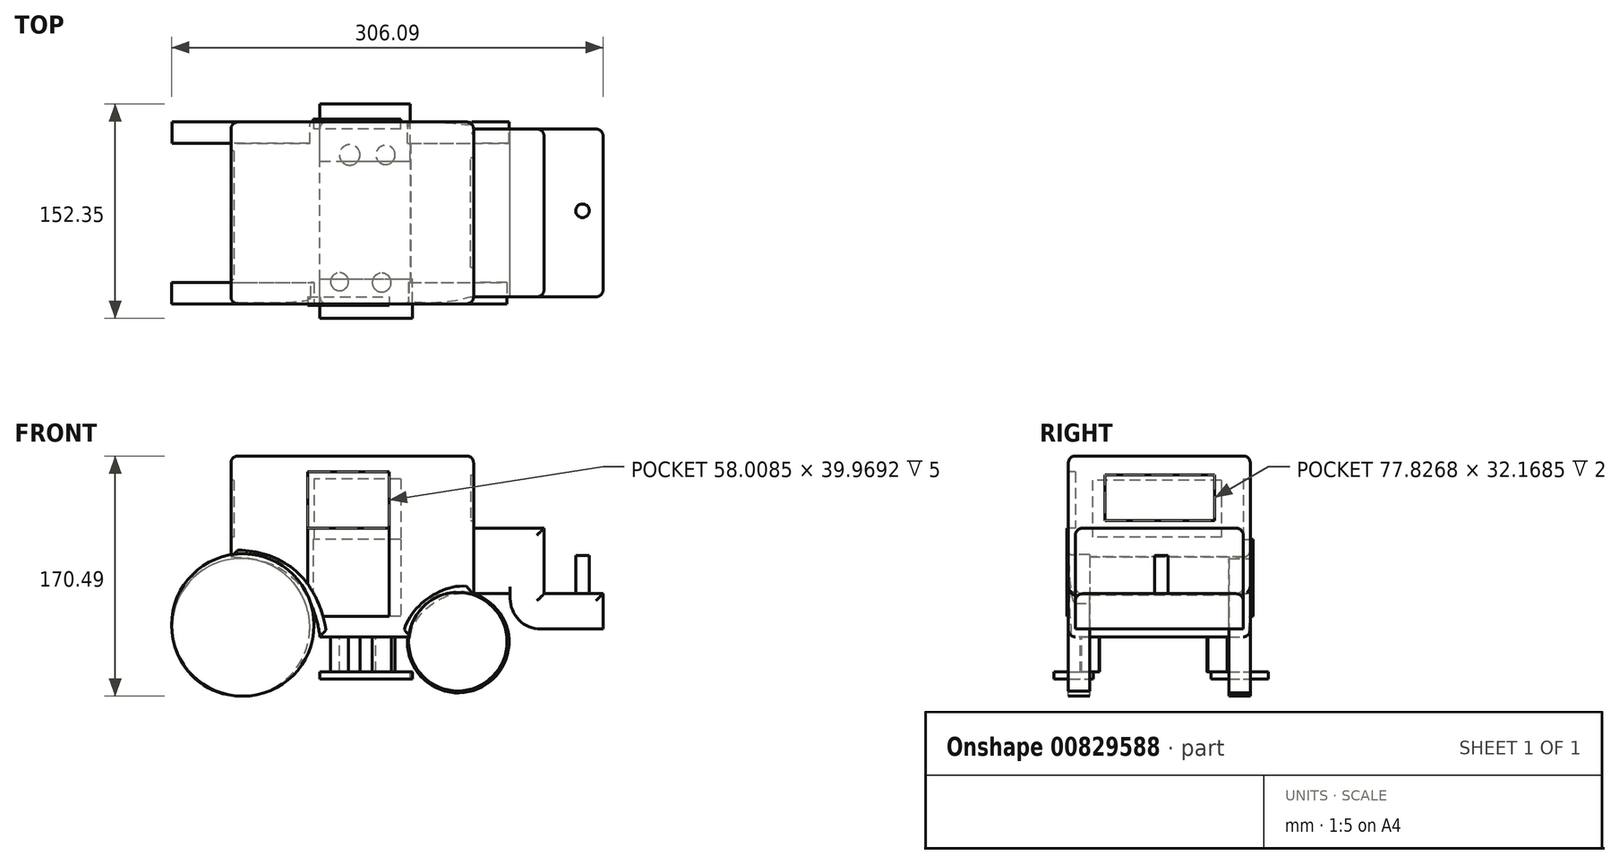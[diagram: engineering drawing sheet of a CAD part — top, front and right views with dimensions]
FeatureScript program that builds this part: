
annotation { "Feature Type Name" : "Feature", "Feature Type Description" : "" }
export const myFeature = defineFeature(function(context is Context, id is Id, definition is map)
    precondition{}
    {
        {
            var Q0;
            Q0=qCreatedBy(makeId("Front.planeOp"),FACE);
            var sketch = newSketch(context, id + "F0", { "sketchPlane" : qUnion([Q0])});
            skLineSegment(sketch, "E0.bottom", {"start": v(-63.14, 51.22) * mm, "end": v(108.92, 51.22) * mm});
            skLineSegment(sketch, "E0.top", {"start": v(-63.14, -77.13) * mm, "end": v(108.92, -77.13) * mm});
            skLineSegment(sketch, "E0.left", {"start": v(-63.14, 51.22) * mm, "end": v(-63.14, -77.13) * mm});
            skLineSegment(sketch, "E0.right", {"start": v(108.92, 51.22) * mm, "end": v(108.92, -77.13) * mm});
            skFitSpline(sketch, "E1", {"points": [v(-63.14, -20.5) * mm, v(0, -77.13) * mm], "startDerivative": vector(140.08, 1.65) * mm, "endDerivative": vector(9.7, -72.66) * mm});
            skCircle(sketch, "E2", {"center": v(-56, -70.4) * mm, "radius": 48.82 * mm});
            skFitSpline(sketch, "E3", {"points": [v(64.44, -77.13) * mm, v(108.92, -47.47) * mm], "startDerivative": vector(-2.62, 44.49) * mm, "endDerivative": vector(57.47, -20.94) * mm});
            skSolve(sketch);
        }
        {
            var Q0;
            {var subQ3=sQuery(id+"F0.wireOp",EDGE,"E1");Q0=makeQuery(id+"F0.imprint","IMPRINT",FACE,{"disambiguationData":[TD([[makeQuery(id+"F0.imprint","IMPRINT",EDGE,{"derivedFrom":subQ3}),-1.0]])]});}
            var Q1;
            {var subQ1=sQuery(id+"F0.wireOp",EDGE,"E0.bottom");Q1=makeQuery(id+"F0.imprint","IMPRINT",FACE,{"disambiguationData":[TD([[makeQuery(id+"F0.imprint","IMPRINT",EDGE,{"derivedFrom":subQ1}),-1.0]])]});}
            extrude(context, id + "F1", {"entities" : qUnion([Q0, Q1]), "depth" : 129 * mm, "offsetDistance" : 25 * mm});
        }
        {
            var Q0;
            {var subQ3=sQuery(id+"F0.wireOp",EDGE,"E1");Q0=makeQuery(id+"F0.imprint","IMPRINT",FACE,{"disambiguationData":[TD([[makeQuery(id+"F0.imprint","IMPRINT",EDGE,{"derivedFrom":subQ3}),-1.0]])]});}
            extrude(context, id + "F2", {"entities" : qUnion([Q0]), "operationType" : NewBodyOperationType.REMOVE, "depth" : 218 * mm, "offsetDistance" : 25 * mm});
        }
        {
            var Q0;
            Q0=makeQuery(id+"F1.opExtrude","CAP_FACE",FACE,{"disambiguationData":[OSD([sQuery(id+"F0.wireOp",EDGE,"E0.bottom"),sQuery(id+"F0.wireOp",EDGE,"E0.top"),sQuery(id+"F0.wireOp",EDGE,"E0.left"),sQuery(id+"F0.wireOp",EDGE,"E0.right")])],"isStart":true});
            fillet(context, id + "F3", {"entities" : qUnion([Q0]), "radius" : 5 * mm, "tangentPropagation" : true, "allowEdgeOverflow" : false});
        }
        {
            var Q0;
            Q0=makeQuery(id+"F1.opExtrude","CAP_FACE",FACE,{"disambiguationData":[OSD([sQuery(id+"F0.wireOp",EDGE,"E0.bottom"),sQuery(id+"F0.wireOp",EDGE,"E0.top"),sQuery(id+"F0.wireOp",EDGE,"E0.left"),sQuery(id+"F0.wireOp",EDGE,"E0.right")])],"isStart":false});
            fillet(context, id + "F4", {"entities" : qUnion([Q0]), "radius" : 5 * mm, "tangentPropagation" : true, "allowEdgeOverflow" : false});
        }
        {
            var Q0;
            Q0=makeQuery(id+"F1.opExtrude","SWEPT_FACE",FACE,{"disambiguationData":[OSD([sQuery(id+"F0.wireOp",EDGE,"E0.bottom")])]});
            fillet(context, id + "F5", {"entities" : qUnion([Q0]), "radius" : 5 * mm, "tangentPropagation" : true, "allowEdgeOverflow" : false});
        }
        {
            var Q0;
            {var subQ0=sQuery(id+"F0.wireOp",EDGE,"E0.left");var subQ1=sQuery(id+"F0.wireOp",EDGE,"E0.top");var subQ2=makeQuery(id+"F0.imprint","INTERSECT",VERTEX,{"derivedFrom":[subQ1,subQ0]});Q0=makeQuery(id+"F0.imprint","IMPRINT",FACE,{"disambiguationData":[TD([[makeQuery(id+"F0.imprint","IMPRINT",EDGE,{"disambiguationData":[TD([[subQ2,-1.0]])],"derivedFrom":subQ1}),-1.0]])]});}
            var Q1;
            {var subQ0=sQuery(id+"F0.wireOp",EDGE,"E0.left");var subQ1=sQuery(id+"F0.wireOp",EDGE,"E0.top");var subQ2=makeQuery(id+"F0.imprint","INTERSECT",VERTEX,{"derivedFrom":[subQ1,subQ0]});Q1=makeQuery(id+"F0.imprint","IMPRINT",FACE,{"disambiguationData":[TD([[makeQuery(id+"F0.imprint","IMPRINT",EDGE,{"disambiguationData":[TD([[subQ2,-1.0]])],"derivedFrom":subQ1}),1.0]])]});}
            extrude(context, id + "F6", {"entities" : qUnion([Q0, Q1]), "depth" : 15 * mm, "offsetDistance" : 25 * mm});
        }
        {
            var Q0;
            Q0=qCreatedBy(makeId("Front.planeOp"),FACE);
            var sketch = newSketch(context, id + "F7", { "sketchPlane" : qUnion([Q0])});
            skCircle(sketch, "E4", {"center": v(98.04, -80.89) * mm, "radius": 36 * mm});
            skSolve(sketch);
        }
        {
            var Q0;
            Q0=makeQuery(id+"F7.imprint","IMPRINT",FACE,{"disambiguationData":[TD([[makeQuery(id+"F7.imprint","IMPRINT",EDGE,{"derivedFrom":sQuery(id+"F7.wireOp",EDGE,"E4")}),1.0]])]});
            extrude(context, id + "F8", {"entities" : qUnion([Q0]), "operationType" : NewBodyOperationType.ADD, "depth" : 15 * mm, "offsetDistance" : 25 * mm});
        }
        {
            var Q0;
            Q0=makeQuery(id+"F1.opExtrude","CAP_FACE",FACE,{"disambiguationData":[OSD([sQuery(id+"F0.wireOp",EDGE,"E0.bottom"),sQuery(id+"F0.wireOp",EDGE,"E0.top"),sQuery(id+"F0.wireOp",EDGE,"E0.left"),sQuery(id+"F0.wireOp",EDGE,"E0.right"),sQuery(id+"F0.wireOp",EDGE,"E2"),sQuery(id+"F0.wireOp",EDGE,"E3")])],"isStart":false});
            var sketch = newSketch(context, id + "F9", { "sketchPlane" : qUnion([Q0])});
            skCircle(sketch, "E5", {"center": v(-54.73, -68.73) * mm, "radius": 50.55 * mm});
            skSolve(sketch);
        }
        {
            var Q0;
            Q0=makeQuery(id+"F9.imprint","IMPRINT",FACE,{"disambiguationData":[TD([[makeQuery(id+"F9.imprint","IMPRINT",EDGE,{"derivedFrom":sQuery(id+"F9.wireOp",EDGE,"E5")}),1.0]])]});
            extrude(context, id + "F10", {"entities" : qUnion([Q0]), "operationType" : NewBodyOperationType.ADD, "oppositeDirection" : true, "depth" : 15 * mm, "offsetDistance" : 25 * mm});
        }
        {
            var Q0;
            Q0=makeQuery(id+"F1.opExtrude","CAP_FACE",FACE,{"disambiguationData":[OSD([sQuery(id+"F0.wireOp",EDGE,"E0.bottom"),sQuery(id+"F0.wireOp",EDGE,"E0.top"),sQuery(id+"F0.wireOp",EDGE,"E0.left"),sQuery(id+"F0.wireOp",EDGE,"E0.right"),sQuery(id+"F0.wireOp",EDGE,"E2"),sQuery(id+"F0.wireOp",EDGE,"E3")])],"isStart":false});
            var sketch = newSketch(context, id + "F11", { "sketchPlane" : qUnion([Q0])});
            skCircle(sketch, "E6", {"center": v(97.8, -80.55) * mm, "radius": 34.93 * mm});
            skSolve(sketch);
        }
        {
            var Q0;
            Q0=makeQuery(id+"F11.imprint","IMPRINT",FACE,{"disambiguationData":[TD([[makeQuery(id+"F11.imprint","IMPRINT",EDGE,{"derivedFrom":sQuery(id+"F11.wireOp",EDGE,"E6")}),1.0]])]});
            extrude(context, id + "F12", {"entities" : qUnion([Q0]), "operationType" : NewBodyOperationType.ADD, "oppositeDirection" : true, "depth" : 15 * mm, "offsetDistance" : 25 * mm});
        }
        {
            var Q0;
            Q0=makeQuery(id+"F1.opExtrude","CAP_FACE",FACE,{"disambiguationData":[OSD([sQuery(id+"F0.wireOp",EDGE,"E0.bottom"),sQuery(id+"F0.wireOp",EDGE,"E0.top"),sQuery(id+"F0.wireOp",EDGE,"E0.left"),sQuery(id+"F0.wireOp",EDGE,"E0.right"),sQuery(id+"F0.wireOp",EDGE,"E2"),sQuery(id+"F0.wireOp",EDGE,"E3")])],"isStart":false});
            var sketch = newSketch(context, id + "F13", { "sketchPlane" : qUnion([Q0])});
            skLineSegment(sketch, "E7.bottom", {"start": v(-8.85, 39.97) * mm, "end": v(49.16, 39.97) * mm});
            skLineSegment(sketch, "E7.top", {"start": v(-8.85, 0) * mm, "end": v(49.16, 0) * mm});
            skLineSegment(sketch, "E7.left", {"start": v(-8.85, 39.97) * mm, "end": v(-8.85, 0) * mm});
            skLineSegment(sketch, "E7.right", {"start": v(49.16, 39.97) * mm, "end": v(49.16, 0) * mm});
            skSolve(sketch);
        }
        {
            var Q0;
            Q0=makeQuery(id+"F13.imprint","IMPRINT",FACE,{"disambiguationData":[TD([[makeQuery(id+"F13.imprint","IMPRINT",EDGE,{"derivedFrom":sQuery(id+"F13.wireOp",EDGE,"E7.bottom")}),-1.0]])]});
            extrude(context, id + "F14", {"entities" : qUnion([Q0]), "operationType" : NewBodyOperationType.REMOVE, "oppositeDirection" : true, "depth" : 5 * mm, "offsetDistance" : 25 * mm});
        }
        {
            var Q0;
            Q0=makeQuery(id+"F1.opExtrude","CAP_FACE",FACE,{"disambiguationData":[OSD([sQuery(id+"F0.wireOp",EDGE,"E0.bottom"),sQuery(id+"F0.wireOp",EDGE,"E0.top"),sQuery(id+"F0.wireOp",EDGE,"E0.left"),sQuery(id+"F0.wireOp",EDGE,"E0.right"),sQuery(id+"F0.wireOp",EDGE,"E2"),sQuery(id+"F0.wireOp",EDGE,"E3")])],"isStart":false});
            var sketch = newSketch(context, id + "F15", { "sketchPlane" : qUnion([Q0])});
            skLineSegment(sketch, "E8", {"start": v(-8.85, 0) * mm, "end": v(-8.85, -39.58) * mm});
            skLineSegment(sketch, "E9", {"start": v(49.16, 0) * mm, "end": v(49.16, -62.53) * mm});
            skLineSegment(sketch, "E10", {"start": v(49.16, -62.53) * mm, "end": v(2.09, -62.53) * mm});
            skSolve(sketch);
        }
        {
            var Q0;
            {var subQ1=sQuery(id+"F15.wireOp",EDGE,"E8");Q0=makeQuery(id+"F15.imprint","IMPRINT",FACE,{"disambiguationData":[TD([[makeQuery(id+"F15.imprint","IMPRINT",EDGE,{"derivedFrom":subQ1}),1.0]])]});}
            extrude(context, id + "F16", {"entities" : qUnion([Q0]), "operationType" : NewBodyOperationType.ADD, "depth" : 1 * mm, "offsetDistance" : 25 * mm});
        }
        {
            var Q0;
            Q0=makeQuery(id+"F1.opExtrude","CAP_FACE",FACE,{"disambiguationData":[OSD([sQuery(id+"F0.wireOp",EDGE,"E0.bottom"),sQuery(id+"F0.wireOp",EDGE,"E0.top"),sQuery(id+"F0.wireOp",EDGE,"E0.left"),sQuery(id+"F0.wireOp",EDGE,"E0.right"),sQuery(id+"F0.wireOp",EDGE,"E2"),sQuery(id+"F0.wireOp",EDGE,"E3")])],"isStart":false});
            var sketch = newSketch(context, id + "F17", { "sketchPlane" : qUnion([Q0])});
            skFitSpline(sketch, "E11", {"points": [v(-58.14, -15.56) * mm, v(-8.85, 39.97) * mm], "startDerivative": vector(207, -25) * mm, "endDerivative": vector(147.87, 73.92) * mm});
            skFitSpline(sketch, "E12", {"points": [v(53.1, 39.97) * mm, v(103.92, -41.26) * mm], "startDerivative": vector(152.47, -4.07) * mm, "endDerivative": vector(89.96, -3.1) * mm});
            skFitSpline(sketch, "E13", {"points": [v(49.16, -62.53) * mm, v(103.92, 0) * mm], "startDerivative": vector(164.3, 21.28) * mm, "endDerivative": vector(164.3, -26.3) * mm});
            skFitSpline(sketch, "E14", {"points": [v(-58.14, 46.22) * mm, v(-8.85, 0) * mm], "startDerivative": vector(107.32, -14.38) * mm, "endDerivative": vector(128.4, 68.32) * mm});
            skFitSpline(sketch, "E15", {"points": [v(49.16, -25.03) * mm, v(103.92, 46.22) * mm], "startDerivative": vector(103.06, -10.14) * mm, "endDerivative": vector(147.4, 54.93) * mm});
            skSolve(sketch);
        }
        {
            var Q0;
            Q0=sQuery(id+"F17.wireOp",EDGE,"E11");
            extrude(context, id + "F18", {"bodyType" : ToolBodyType.SURFACE, "surfaceEntities" : qUnion([Q0]), "depth" : 2 * mm, "offsetDistance" : 25 * mm});
        }
        {
            var Q0;
            Q0=sQuery(id+"F17.wireOp",EDGE,"E14");
            extrude(context, id + "F19", {"bodyType" : ToolBodyType.SURFACE, "surfaceEntities" : qUnion([Q0]), "depth" : 2 * mm, "offsetDistance" : 25 * mm});
        }
        {
            var Q0;
            Q0=sQuery(id+"F17.wireOp",EDGE,"E15");
            extrude(context, id + "F20", {"bodyType" : ToolBodyType.SURFACE, "surfaceEntities" : qUnion([Q0]), "depth" : 2 * mm, "offsetDistance" : 25 * mm});
        }
        {
            var Q0;
            Q0=sQuery(id+"F17.wireOp",EDGE,"E13");
            extrude(context, id + "F21", {"bodyType" : ToolBodyType.SURFACE, "surfaceEntities" : qUnion([Q0]), "depth" : 2 * mm, "offsetDistance" : 25 * mm});
        }
        {
            var Q0;
            Q0=sQuery(id+"F17.wireOp",EDGE,"E12");
            extrude(context, id + "F22", {"bodyType" : ToolBodyType.SURFACE, "surfaceEntities" : qUnion([Q0]), "depth" : 2 * mm, "offsetDistance" : 25 * mm});
        }
        {
            var Q0;
            Q0=makeQuery(id+"F1.opExtrude","SWEPT_FACE",FACE,{"disambiguationData":[OSD([sQuery(id+"F0.wireOp",EDGE,"E0.right")])]});
            var sketch = newSketch(context, id + "F23", { "sketchPlane" : qUnion([Q0])});
            skLineSegment(sketch, "E16.bottom", {"start": v(-124, 0) * mm, "end": v(-5, 0) * mm});
            skLineSegment(sketch, "E16.top", {"start": v(-124, -46.56) * mm, "end": v(-5, -46.56) * mm});
            skLineSegment(sketch, "E16.left", {"start": v(-124, 0) * mm, "end": v(-124, -46.56) * mm});
            skLineSegment(sketch, "E16.right", {"start": v(-5, 0) * mm, "end": v(-5, -46.56) * mm});
            skSolve(sketch);
        }
        {
            var Q0;
            Q0=makeQuery(id+"F23.imprint","IMPRINT",FACE,{"disambiguationData":[TD([[makeQuery(id+"F23.imprint","IMPRINT",EDGE,{"derivedFrom":sQuery(id+"F23.wireOp",EDGE,"E16.bottom")}),-1.0]])]});
            extrude(context, id + "F24", {"entities" : qUnion([Q0]), "operationType" : NewBodyOperationType.ADD, "depth" : 50 * mm, "offsetDistance" : 25 * mm});
        }
        {
            var Q0;
            Q0=makeQuery(id+"F24.opExtrude","SWEPT_FACE",FACE,{"disambiguationData":[OSD([sQuery(id+"F23.wireOp",EDGE,"E16.top")])]});
            var sketch = newSketch(context, id + "F25", { "sketchPlane" : qUnion([Q0])});
            skLineSegment(sketch, "E17.bottom", {"start": v(134.85, 124) * mm, "end": v(200.81, 124) * mm});
            skLineSegment(sketch, "E17.top", {"start": v(134.85, 5) * mm, "end": v(200.81, 5) * mm});
            skLineSegment(sketch, "E17.left", {"start": v(134.85, 124) * mm, "end": v(134.85, 5) * mm});
            skLineSegment(sketch, "E17.right", {"start": v(200.81, 124) * mm, "end": v(200.81, 5) * mm});
            skSolve(sketch);
        }
        {
            var Q0;
            Q0 = qSketchRegion(id + "F25", true);
            extrude(context, id + "F26", {"entities" : qUnion([Q0]), "operationType" : NewBodyOperationType.ADD, "depth" : 25 * mm, "offsetDistance" : 25 * mm});
        }
        {
            var Q0;
            Q0=makeQuery(id+"F26.opExtrude","CAP_EDGE",EDGE,{"disambiguationData":[OSD([sQuery(id+"F25.wireOp",EDGE,"E17.left")])],"isStart":false});
            fillet(context, id + "F27", {"entities" : qUnion([Q0]), "radius" : 21.73 * mm, "tangentPropagation" : true, "allowEdgeOverflow" : false});
        }
        {
            var Q0;
            Q0=makeQuery(id+"F24.opExtrude","SWEPT_EDGE",EDGE,{"disambiguationData":[OSD([sQuery(id+"F0.wireOp",EDGE,"E0.right"),sQuery(id+"F23.wireOp",EDGE,"E16.bottom"),sQuery(id+"F23.wireOp",EDGE,"E16.left")])]});
            var Q1;
            Q1=makeQuery(id+"F24.opExtrude","CAP_EDGE",EDGE,{"disambiguationData":[OSD([sQuery(id+"F23.wireOp",EDGE,"E16.left")])],"isStart":false});
            var Q2;
            Q2=makeQuery(id+"F26.opExtrude","CAP_EDGE",EDGE,{"disambiguationData":[OSD([sQuery(id+"F25.wireOp",EDGE,"E17.bottom")])],"isStart":true});
            var Q3;
            Q3=makeQuery(id+"F26.opExtrude","SWEPT_EDGE",EDGE,{"disambiguationData":[OSD([sQuery(id+"F25.wireOp",EDGE,"E17.bottom"),sQuery(id+"F25.wireOp",EDGE,"E17.right")])]});
            var Q4;
            Q4=makeQuery(id+"F24.opExtrude","SWEPT_EDGE",EDGE,{"disambiguationData":[OSD([sQuery(id+"F0.wireOp",EDGE,"E0.right"),sQuery(id+"F23.wireOp",EDGE,"E16.top"),sQuery(id+"F23.wireOp",EDGE,"E16.left")])]});
            fillet(context, id + "F28", {"entities" : qUnion([Q0, Q1, Q2, Q3, Q4]), "radius" : 5 * mm, "tangentPropagation" : true, "allowEdgeOverflow" : false});
        }
        {
            var Q0;
            Q0=makeQuery(id+"F24.opExtrude","SWEPT_EDGE",EDGE,{"disambiguationData":[OSD([sQuery(id+"F0.wireOp",EDGE,"E0.right"),sQuery(id+"F23.wireOp",EDGE,"E16.bottom"),sQuery(id+"F23.wireOp",EDGE,"E16.right")])]});
            var Q1;
            Q1=makeQuery(id+"F24.opExtrude","CAP_EDGE",EDGE,{"disambiguationData":[OSD([sQuery(id+"F23.wireOp",EDGE,"E16.right")])],"isStart":false});
            var Q2;
            Q2=makeQuery(id+"F26.opExtrude","CAP_EDGE",EDGE,{"disambiguationData":[OSD([sQuery(id+"F25.wireOp",EDGE,"E17.top")])],"isStart":true});
            var Q3;
            Q3=makeQuery(id+"F26.opExtrude","SWEPT_EDGE",EDGE,{"disambiguationData":[OSD([sQuery(id+"F25.wireOp",EDGE,"E17.top"),sQuery(id+"F25.wireOp",EDGE,"E17.right")])]});
            var Q4;
            Q4=makeQuery(id+"F24.opExtrude","SWEPT_EDGE",EDGE,{"disambiguationData":[OSD([sQuery(id+"F23.wireOp",EDGE,"E16.top"),sQuery(id+"F23.wireOp",EDGE,"E16.right")])]});
            fillet(context, id + "F29", {"entities" : qUnion([Q0, Q1, Q2, Q3, Q4]), "radius" : 5 * mm, "tangentPropagation" : true, "allowEdgeOverflow" : false});
        }
        {
            var Q0;
            Q0=makeQuery(id+"F26.opExtrude","CAP_FACE",FACE,{"disambiguationData":[OSD([sQuery(id+"F25.wireOp",EDGE,"E17.bottom"),sQuery(id+"F25.wireOp",EDGE,"E17.top"),sQuery(id+"F25.wireOp",EDGE,"E17.left"),sQuery(id+"F25.wireOp",EDGE,"E17.right")])],"isStart":true});
            var sketch = newSketch(context, id + "F30", { "sketchPlane" : qUnion([Q0])});
            skCircle(sketch, "E18", {"center": v(186.19, -62.99) * mm, "radius": 4.82 * mm});
            skSolve(sketch);
        }
        {
            var Q0;
            Q0=makeQuery(id+"F30.imprint","IMPRINT",FACE,{"disambiguationData":[TD([[makeQuery(id+"F30.imprint","IMPRINT",EDGE,{"derivedFrom":sQuery(id+"F30.wireOp",EDGE,"E18")}),1.0]])]});
            extrude(context, id + "F31", {"entities" : qUnion([Q0]), "operationType" : NewBodyOperationType.ADD, "depth" : 27 * mm, "offsetDistance" : 25 * mm});
        }
        {
            var Q0;
            Q0=makeQuery(id+"F1.opExtrude","SWEPT_FACE",FACE,{"disambiguationData":[OSD([sQuery(id+"F0.wireOp",EDGE,"E0.top")])]});
            var sketch = newSketch(context, id + "F32", { "sketchPlane" : qUnion([Q0])});
            skCircle(sketch, "E19", {"center": v(13.9, 113.31) * mm, "radius": 6.36 * mm});
            skCircle(sketch, "E20", {"center": v(43.8, 113.91) * mm, "radius": 6.69 * mm});
            skSolve(sketch);
        }
        {
            var Q0;
            Q0=makeQuery(id+"F32.imprint","IMPRINT",FACE,{"disambiguationData":[TD([[makeQuery(id+"F32.imprint","IMPRINT",EDGE,{"derivedFrom":sQuery(id+"F32.wireOp",EDGE,"E19")}),1.0]])]});
            var Q1;
            Q1=makeQuery(id+"F32.imprint","IMPRINT",FACE,{"disambiguationData":[TD([[makeQuery(id+"F32.imprint","IMPRINT",EDGE,{"derivedFrom":sQuery(id+"F32.wireOp",EDGE,"E20")}),1.0]])]});
            extrude(context, id + "F33", {"entities" : qUnion([Q0, Q1]), "operationType" : NewBodyOperationType.ADD, "depth" : 25 * mm, "offsetDistance" : 25 * mm});
        }
        {
            var Q0;
            Q0=makeQuery(id+"F33.opExtrude","CAP_FACE",FACE,{"disambiguationData":[OSD([sQuery(id+"F32.wireOp",EDGE,"E19")])],"isStart":false});
            var sketch = newSketch(context, id + "F34", { "sketchPlane" : qUnion([Q0])});
            skLineSegment(sketch, "E21.bottom", {"start": v(0, 139.4) * mm, "end": v(65.44, 139.4) * mm});
            skLineSegment(sketch, "E21.top", {"start": v(0, 111.27) * mm, "end": v(65.44, 111.27) * mm});
            skLineSegment(sketch, "E21.left", {"start": v(0, 139.4) * mm, "end": v(0, 111.27) * mm});
            skLineSegment(sketch, "E21.right", {"start": v(65.44, 139.4) * mm, "end": v(65.44, 111.27) * mm});
            skSolve(sketch);
        }
        {
            var Q0;
            Q0 = qSketchRegion(id + "F34", true);
            extrude(context, id + "F35", {"entities" : qUnion([Q0]), "operationType" : NewBodyOperationType.ADD, "depth" : 5 * mm, "offsetDistance" : 25 * mm});
        }
        {
            var Q0;
            Q0=makeQuery(id+"F1.opExtrude","SWEPT_FACE",FACE,{"disambiguationData":[OSD([sQuery(id+"F0.wireOp",EDGE,"E0.left")])]});
            var sketch = newSketch(context, id + "F36", { "sketchPlane" : qUnion([Q0])});
            skLineSegment(sketch, "E22.bottom", {"start": v(20.5, 33.98) * mm, "end": v(111.82, 33.98) * mm});
            skLineSegment(sketch, "E22.top", {"start": v(20.5, -6.5) * mm, "end": v(111.82, -6.5) * mm});
            skLineSegment(sketch, "E22.left", {"start": v(20.5, 33.98) * mm, "end": v(20.5, -6.5) * mm});
            skLineSegment(sketch, "E22.right", {"start": v(111.82, 33.98) * mm, "end": v(111.82, -6.5) * mm});
            skSolve(sketch);
        }
        {
            var Q0;
            Q0=makeQuery(id+"F36.imprint","IMPRINT",FACE,{"disambiguationData":[TD([[makeQuery(id+"F36.imprint","IMPRINT",EDGE,{"derivedFrom":sQuery(id+"F36.wireOp",EDGE,"E22.bottom")}),-1.0]])]});
            extrude(context, id + "F37", {"entities" : qUnion([Q0]), "operationType" : NewBodyOperationType.REMOVE, "oppositeDirection" : true, "depth" : 2 * mm, "offsetDistance" : 25 * mm});
        }
        {
            var Q0;
            Q0=makeQuery(id+"F1.opExtrude","CAP_FACE",FACE,{"disambiguationData":[OSD([sQuery(id+"F0.wireOp",EDGE,"E0.bottom"),sQuery(id+"F0.wireOp",EDGE,"E0.top"),sQuery(id+"F0.wireOp",EDGE,"E0.left"),sQuery(id+"F0.wireOp",EDGE,"E0.right"),sQuery(id+"F0.wireOp",EDGE,"E2"),sQuery(id+"F0.wireOp",EDGE,"E3")])],"isStart":true});
            var sketch = newSketch(context, id + "F38", { "sketchPlane" : qUnion([Q0])});
            skLineSegment(sketch, "E23.bottom", {"start": v(-57.39, 35.01) * mm, "end": v(4.35, 35.01) * mm});
            skLineSegment(sketch, "E23.top", {"start": v(-57.39, -8.05) * mm, "end": v(4.35, -8.05) * mm});
            skLineSegment(sketch, "E23.left", {"start": v(-57.39, 35.01) * mm, "end": v(-57.39, -8.05) * mm});
            skLineSegment(sketch, "E23.right", {"start": v(4.35, 35.01) * mm, "end": v(4.35, -8.05) * mm});
            skLineSegment(sketch, "E24.bottom", {"start": v(-57.39, -8.05) * mm, "end": v(4.87, -8.05) * mm});
            skLineSegment(sketch, "E24.top", {"start": v(-57.39, -62.53) * mm, "end": v(4.87, -62.53) * mm});
            skLineSegment(sketch, "E24.left", {"start": v(-57.39, -8.05) * mm, "end": v(-57.39, -62.53) * mm});
            skLineSegment(sketch, "E24.right", {"start": v(4.87, -8.05) * mm, "end": v(4.87, -62.53) * mm});
            skSolve(sketch);
        }
        {
            var Q0;
            Q0=makeQuery(id+"F38.imprint","IMPRINT",FACE,{"disambiguationData":[TD([[makeQuery(id+"F38.imprint","IMPRINT",EDGE,{"derivedFrom":sQuery(id+"F38.wireOp",EDGE,"E23.bottom")}),-1.0]])]});
            extrude(context, id + "F39", {"entities" : qUnion([Q0]), "operationType" : NewBodyOperationType.REMOVE, "oppositeDirection" : true, "depth" : 5 * mm, "offsetDistance" : 25 * mm});
        }
        {
            var Q0;
            {var subQ0=sQuery(id+"F38.wireOp",EDGE,"E24.left");Q0=makeQuery(id+"F38.imprint","IMPRINT",FACE,{"disambiguationData":[TD([[makeQuery(id+"F38.imprint","IMPRINT",EDGE,{"derivedFrom":subQ0}),1.0]])]});}
            extrude(context, id + "F40", {"entities" : qUnion([Q0]), "operationType" : NewBodyOperationType.ADD, "depth" : 2 * mm, "offsetDistance" : 25 * mm});
        }
        {
            var Q0;
            {var subQ0=sQuery(id+"F0.wireOp",EDGE,"E0.right");Q0=makeQuery(id+"F24.boolean.opBoolean","SPLIT",FACE,{"disambiguationData":[TD([makeQuery(id+"F3.opFillet","BLEND_FACE",FACE,{"disambiguationData":[OSD([subQ0])]})])],"derivedFrom":makeQuery(id+"F1.opExtrude","SWEPT_FACE",FACE,{"disambiguationData":[OSD([subQ0])]})});}
            var sketch = newSketch(context, id + "F41", { "sketchPlane" : qUnion([Q0])});
            skLineSegment(sketch, "E25.bottom", {"start": v(-103.05, 37.6) * mm, "end": v(-25.22, 37.6) * mm});
            skLineSegment(sketch, "E25.top", {"start": v(-103.05, 5.44) * mm, "end": v(-25.22, 5.44) * mm});
            skLineSegment(sketch, "E25.left", {"start": v(-103.05, 37.6) * mm, "end": v(-103.05, 5.44) * mm});
            skLineSegment(sketch, "E25.right", {"start": v(-25.22, 37.6) * mm, "end": v(-25.22, 5.44) * mm});
            skSolve(sketch);
        }
        {
            var Q0;
            Q0=makeQuery(id+"F41.imprint","IMPRINT",FACE,{"disambiguationData":[TD([[makeQuery(id+"F41.imprint","IMPRINT",EDGE,{"derivedFrom":sQuery(id+"F41.wireOp",EDGE,"E25.bottom")}),-1.0]])]});
            extrude(context, id + "F42", {"entities" : qUnion([Q0]), "operationType" : NewBodyOperationType.REMOVE, "oppositeDirection" : true, "depth" : 2 * mm, "offsetDistance" : 25 * mm});
        }
        {
            var Q0;
            Q0=makeQuery(id+"F1.opExtrude","SWEPT_FACE",FACE,{"disambiguationData":[OSD([sQuery(id+"F0.wireOp",EDGE,"E0.top")])]});
            var sketch = newSketch(context, id + "F43", { "sketchPlane" : qUnion([Q0])});
            skCircle(sketch, "E26", {"center": v(46.5, 23.33) * mm, "radius": 6.81 * mm});
            skCircle(sketch, "E27", {"center": v(21.07, 23.33) * mm, "radius": 7.3 * mm});
            skSolve(sketch);
        }
        {
            var Q0;
            Q0=makeQuery(id+"F43.imprint","IMPRINT",FACE,{"disambiguationData":[TD([[makeQuery(id+"F43.imprint","IMPRINT",EDGE,{"derivedFrom":sQuery(id+"F43.wireOp",EDGE,"E26")}),1.0]])]});
            var Q1;
            Q1=makeQuery(id+"F43.imprint","IMPRINT",FACE,{"disambiguationData":[TD([[makeQuery(id+"F43.imprint","IMPRINT",EDGE,{"derivedFrom":sQuery(id+"F43.wireOp",EDGE,"E27")}),1.0]])]});
            extrude(context, id + "F44", {"entities" : qUnion([Q0, Q1]), "operationType" : NewBodyOperationType.ADD, "depth" : 25 * mm, "offsetDistance" : 25 * mm});
        }
        {
            var Q0;
            Q0=makeQuery(id+"F44.opExtrude","CAP_FACE",FACE,{"disambiguationData":[OSD([sQuery(id+"F43.wireOp",EDGE,"E26")])],"isStart":false});
            var sketch = newSketch(context, id + "F45", { "sketchPlane" : qUnion([Q0])});
            skLineSegment(sketch, "E28.bottom", {"start": v(0, 27.95) * mm, "end": v(63.95, 27.95) * mm});
            skLineSegment(sketch, "E28.top", {"start": v(0, -12.95) * mm, "end": v(63.95, -12.95) * mm});
            skLineSegment(sketch, "E28.left", {"start": v(0, 27.95) * mm, "end": v(0, -12.95) * mm});
            skLineSegment(sketch, "E28.right", {"start": v(63.95, 27.95) * mm, "end": v(63.95, -12.95) * mm});
            skSolve(sketch);
        }
        {
            var Q0;
            Q0=makeQuery(id+"F45.imprint","IMPRINT",FACE,{"disambiguationData":[TD([[makeQuery(id+"F45.imprint","IMPRINT",EDGE,{"derivedFrom":sQuery(id+"F45.wireOp",EDGE,"E28.top")}),1.0]])]});
            var Q1;
            {var subQ0=sQuery(id+"F45.wireOp",EDGE,"E28.bottom");var subQ1=makeQuery(id+"F44.opExtrude","CAP_EDGE",EDGE,{"disambiguationData":[OSD([sQuery(id+"F43.wireOp",EDGE,"E26")])],"isStart":false});var subQ2=makeQuery(id+"F45.imprint","INTERSECT",VERTEX,{"disambiguationData":[OD(0.0)],"derivedFrom":[subQ1,subQ0]});Q1=makeQuery(id+"F45.imprint","IMPRINT",FACE,{"disambiguationData":[TD([[makeQuery(id+"F45.imprint","IMPRINT",EDGE,{"disambiguationData":[TD([[subQ2,-1.0]])],"derivedFrom":subQ0}),-1.0]])]});}
            extrude(context, id + "F46", {"entities" : qUnion([Q0, Q1]), "operationType" : NewBodyOperationType.ADD, "depth" : 5 * mm, "offsetDistance" : 25 * mm});
        }
        {
            var Q0;
            Q0=makeQuery(id+"F1.opExtrude","CAP_FACE",FACE,{"disambiguationData":[OSD([sQuery(id+"F0.wireOp",EDGE,"E0.bottom"),sQuery(id+"F0.wireOp",EDGE,"E0.top"),sQuery(id+"F0.wireOp",EDGE,"E0.left"),sQuery(id+"F0.wireOp",EDGE,"E0.right"),sQuery(id+"F0.wireOp",EDGE,"E2"),sQuery(id+"F0.wireOp",EDGE,"E3")])],"isStart":true});
            var sketch = newSketch(context, id + "F47", { "sketchPlane" : qUnion([Q0])});
            skFitSpline(sketch, "E29", {"points": [v(-103.92, 46.22) * mm, v(-57.39, -22.8) * mm], "startDerivative": vector(83.85, -9.44) * mm, "endDerivative": vector(49.21, 27.49) * mm});
            skFitSpline(sketch, "E30", {"points": [v(58.14, 46.22) * mm, v(4.87, -26.88) * mm], "startDerivative": vector(0, -106.3) * mm, "endDerivative": vector(-8.77, -124.8) * mm});
            skFitSpline(sketch, "E31", {"points": [v(-15.33, 46.22) * mm, v(58.14, 0) * mm], "startDerivative": vector(134.82, -9.44) * mm, "endDerivative": vector(92.14, 19.99) * mm});
            skFitSpline(sketch, "E32", {"points": [v(-98.1, -41.26) * mm, v(-57.39, 46.22) * mm], "startDerivative": vector(91.22, 63.23) * mm, "endDerivative": vector(119.9, 89.28) * mm});
            skFitSpline(sketch, "E33", {"points": [v(43.95, -17.32) * mm, v(29.6, 43.08) * mm], "startDerivative": vector(-44.34, 7.11) * mm, "endDerivative": vector(-13.09, 54.97) * mm});
            skSolve(sketch);
        }
        {
            var Q0;
            {var subQ13=sQuery(id+"F38.wireOp",EDGE,"E24.top");var subQ14=makeQuery(id+"F40.opExtrude","CAP_EDGE",EDGE,{"disambiguationData":[OSD([subQ13])],"isStart":true});Q0=makeQuery(id+"F47.imprint","IMPRINT",FACE,{"disambiguationData":[TD([[makeQuery(id+"F47.imprint","IMPRINT",EDGE,{"derivedFrom":subQ14}),-1.0]])]});}
            var Q1;
            Q1=sQuery(id+"F47.wireOp",EDGE,"E30");
            extrude(context, id + "F48", {"entities" : qUnion([Q0]), "bodyType" : ToolBodyType.SURFACE, "surfaceOperationType" : NewSurfaceOperationType.ADD, "surfaceEntities" : qUnion([Q1]), "depth" : 2 * mm, "offsetDistance" : 25 * mm});
        }
        {
            var Q0;
            Q0=sQuery(id+"F47.wireOp",EDGE,"E33");
            extrude(context, id + "F49", {"bodyType" : ToolBodyType.SURFACE, "surfaceEntities" : qUnion([Q0]), "depth" : 2 * mm, "offsetDistance" : 25 * mm});
        }
        {
            var Q0;
            Q0=sQuery(id+"F47.wireOp",EDGE,"E31");
            extrude(context, id + "F50", {"bodyType" : ToolBodyType.SURFACE, "surfaceEntities" : qUnion([Q0]), "depth" : 2 * mm, "offsetDistance" : 25 * mm});
        }
        {
            var Q0;
            Q0=sQuery(id+"F47.wireOp",EDGE,"E32");
            extrude(context, id + "F51", {"bodyType" : ToolBodyType.SURFACE, "surfaceEntities" : qUnion([Q0]), "depth" : 2 * mm, "offsetDistance" : 25 * mm});
        }
        {
            var Q0;
            Q0=sQuery(id+"F47.wireOp",EDGE,"E29");
            extrude(context, id + "F52", {"bodyType" : ToolBodyType.SURFACE, "surfaceEntities" : qUnion([Q0]), "depth" : 2 * mm, "offsetDistance" : 25 * mm});
        }
    });
